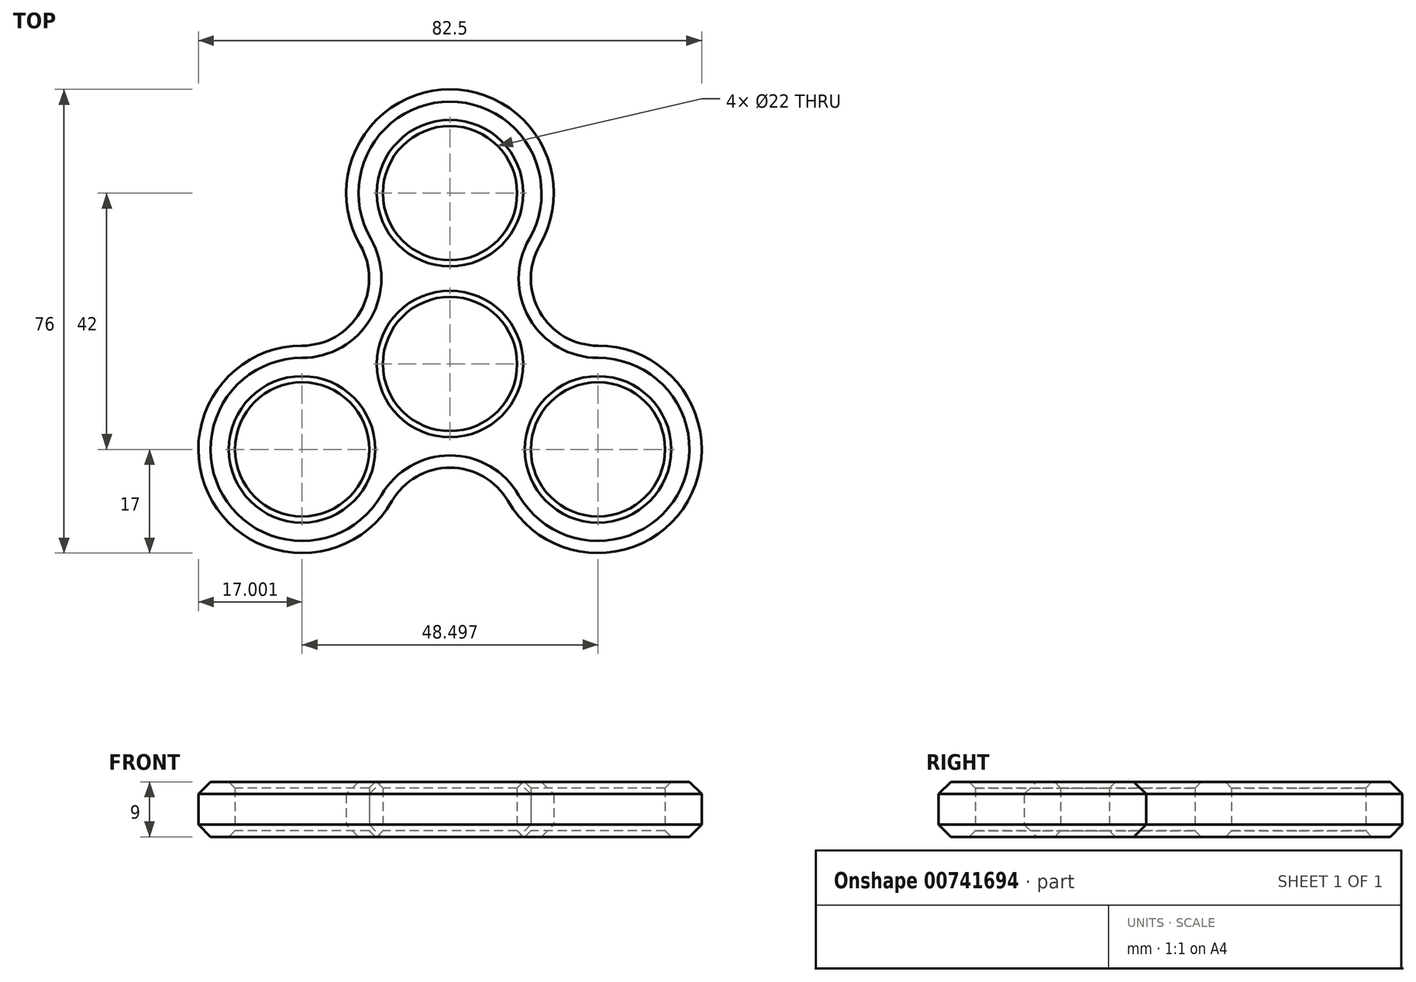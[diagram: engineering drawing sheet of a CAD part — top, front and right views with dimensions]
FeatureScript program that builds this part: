
annotation { "Feature Type Name" : "Feature", "Feature Type Description" : "" }
export const myFeature = defineFeature(function(context is Context, id is Id, definition is map)
    precondition{}
    {
        {
            var Q0;
            Q0=qCreatedBy(makeId("Top.planeOp"),FACE);
            var sketch = newSketch(context, id + "F0", { "sketchPlane" : qUnion([Q0])});
            skCircle(sketch, "E0", {"center": v(0, 28) * mm, "radius": 11 * mm});
            skCircle(sketch, "E1", {"center": v(-24.25, -14) * mm, "radius": 11 * mm});
            skCircle(sketch, "E2", {"center": v(24.25, -14) * mm, "radius": 11 * mm});
            skCircle(sketch, "E3", {"center": v(0, 0) * mm, "radius": 11 * mm});
            skCircle(sketch, "E4", {"center": v(0, 0) * mm, "radius": 28 * mm, "construction": true});
            skLineSegment(sketch, "E5", {"start": v(0, 28) * mm, "end": v(0, 0) * mm, "construction": true});
            skLineSegment(sketch, "E6", {"start": v(0, 0) * mm, "end": v(24.25, -14) * mm, "construction": true});
            skLineSegment(sketch, "E7", {"start": v(0, 0) * mm, "end": v(-24.25, -14) * mm, "construction": true});
            skCircle(sketch, "E8", {"center": v(0, 0) * mm, "radius": 39 * mm, "construction": true});
            skArc(sketch, "E9", {"start": v(-9.53, -22.5) * mm, "mid": v(-38.97, -22.5) * mm, "end": v(-24.25, 3) * mm});
            skArc(sketch, "E10", {"start": v(9.53, -22.5) * mm, "mid": v(38.97, -22.5) * mm, "end": v(24.25, 3) * mm});
            skArc(sketch, "E11", {"start": v(-14.72, 19.5) * mm, "mid": v(0, 45) * mm, "end": v(14.72, 19.5) * mm});
            skLineSegment(sketch, "E12", {"start": v(0, 0) * mm, "end": v(0, -28) * mm, "construction": true});
            skLineSegment(sketch, "E13", {"start": v(0, 0) * mm, "end": v(-24.25, 14) * mm, "construction": true});
            skLineSegment(sketch, "E14", {"start": v(0, 0) * mm, "end": v(24.25, 14) * mm, "construction": true});
            skLineSegment(sketch, "E15", {"start": v(-9.53, -22.5) * mm, "end": v(-9.53, -22.5) * mm});
            skLineSegment(sketch, "E16", {"start": v(-14.72, 19.5) * mm, "end": v(-14.72, 19.5) * mm});
            skLineSegment(sketch, "E17", {"start": v(-24.25, 3) * mm, "end": v(-24.25, 3) * mm});
            skLineSegment(sketch, "E18", {"start": v(14.72, 19.5) * mm, "end": v(14.72, 19.5) * mm});
            skLineSegment(sketch, "E19", {"start": v(24.25, 3) * mm, "end": v(24.25, 3) * mm});
            skLineSegment(sketch, "E20", {"start": v(9.53, -22.5) * mm, "end": v(9.53, -22.5) * mm});
            skArc(sketch, "E21", {"start": v(-14.72, 19.5) * mm, "mid": v(-14.72, 8.5) * mm, "end": v(-24.25, 3) * mm});
            skArc(sketch, "E22", {"start": v(14.72, 19.5) * mm, "mid": v(14.72, 8.5) * mm, "end": v(24.25, 3) * mm});
            skArc(sketch, "E23", {"start": v(9.53, -22.5) * mm, "mid": v(0, -17) * mm, "end": v(-9.53, -22.5) * mm});
            skCircle(sketch, "E24", {"center": v(0, 0) * mm, "radius": 17 * mm, "construction": true});
            skCircle(sketch, "E25", {"center": v(0, 0) * mm, "radius": 45 * mm, "construction": true});
            skSolve(sketch);
        }
        {
            var Q0;
            Q0=qSketchRegion(id+"F0",true);
            extrude(context, id + "F1", {"entities" : qUnion([Q0]), "endBound" : BoundingType.SYMMETRIC, "depth" : 9 * mm, "offsetDistance" : 25 * mm});
        }
        {
            var Q0;
            Q0=qCreatedBy(makeId("Top.planeOp"),FACE);
            var sketch = newSketch(context, id + "F2", { "sketchPlane" : qUnion([Q0])});
            skCircle(sketch, "E26", {"center": v(0, 0) * mm, "radius": 11 * mm});
            skSolve(sketch);
        }
        {
            var Q0;
            Q0=qSketchRegion(id+"F2",true);
            extrude(context, id + "F3", {"entities" : qUnion([Q0]), "operationType" : NewBodyOperationType.REMOVE, "endBound" : BoundingType.THROUGH_ALL, "oppositeDirection" : true, "depth" : 25 * mm, "offsetDistance" : 25 * mm, "hasSecondDirection" : true, "secondDirectionBound" : SecondDirectionBoundingType.THROUGH_ALL, "secondDirectionOppositeDirection" : false, "secondDirectionDepth" : 25 * mm});
        }
        {
            var Q0;
            Q0=makeQuery(id+"F1.opExtrude","CAP_EDGE",EDGE,{"disambiguationData":[OSD([sQuery(id+"F0.wireOp",EDGE,"E9")])],"isStart":false});
            var Q1;
            Q1=makeQuery(id+"F1.opExtrude","CAP_EDGE",EDGE,{"disambiguationData":[OSD([sQuery(id+"F0.wireOp",EDGE,"E9")])],"isStart":true});
            var Q2;
            Q2=makeQuery(id+"F3.boolean.opBoolean","INTERSECT",EDGE,{"derivedFrom":[makeQuery(id+"F1.opExtrude","CAP_FACE",FACE,{"disambiguationData":[OSD([sQuery(id+"F0.wireOp",EDGE,"E0"),sQuery(id+"F0.wireOp",EDGE,"E1"),sQuery(id+"F0.wireOp",EDGE,"E2"),sQuery(id+"F0.wireOp",EDGE,"XNPakRHv-zOhi-0FM5-hTdu-OG3i7tiAVQxY"),sQuery(id+"F0.wireOp",EDGE,"E9"),sQuery(id+"F0.wireOp",EDGE,"dCo0jm6D-gOeC-fFHZ-glrm-1aHonwMQvqJC"),sQuery(id+"F0.wireOp",EDGE,"E10"),sQuery(id+"F0.wireOp",EDGE,"E11"),sQuery(id+"F0.wireOp",EDGE,"YkruY3tB-21v4-OKZR-qZbx-QCQuqMLywjzG"),sQuery(id+"F0.wireOp",EDGE,"SekSoQT0-foV7-ICcH-uNWv-8Mtw90ad5pJT"),sQuery(id+"F0.wireOp",EDGE,"o91gRGPa-Ibxz-ax7s-b3tE-83rfG7TcEAhW"),sQuery(id+"F0.wireOp",EDGE,"bdXiWe1d-0TL7-GA1S-cq4B-UudjERh8iepl")])],"isStart":true}),makeQuery(id+"F3.opExtrude","SWEPT_FACE",FACE,{"disambiguationData":[OSD([sQuery(id+"F2.wireOp",EDGE,"E26")])]})]});
            var Q3;
            Q3=makeQuery(id+"F3.boolean.opBoolean","INTERSECT",EDGE,{"derivedFrom":[makeQuery(id+"F1.opExtrude","CAP_FACE",FACE,{"disambiguationData":[OSD([sQuery(id+"F0.wireOp",EDGE,"E0"),sQuery(id+"F0.wireOp",EDGE,"E1"),sQuery(id+"F0.wireOp",EDGE,"E2"),sQuery(id+"F0.wireOp",EDGE,"XNPakRHv-zOhi-0FM5-hTdu-OG3i7tiAVQxY"),sQuery(id+"F0.wireOp",EDGE,"E9"),sQuery(id+"F0.wireOp",EDGE,"dCo0jm6D-gOeC-fFHZ-glrm-1aHonwMQvqJC"),sQuery(id+"F0.wireOp",EDGE,"E10"),sQuery(id+"F0.wireOp",EDGE,"E11"),sQuery(id+"F0.wireOp",EDGE,"YkruY3tB-21v4-OKZR-qZbx-QCQuqMLywjzG"),sQuery(id+"F0.wireOp",EDGE,"SekSoQT0-foV7-ICcH-uNWv-8Mtw90ad5pJT"),sQuery(id+"F0.wireOp",EDGE,"o91gRGPa-Ibxz-ax7s-b3tE-83rfG7TcEAhW"),sQuery(id+"F0.wireOp",EDGE,"bdXiWe1d-0TL7-GA1S-cq4B-UudjERh8iepl")])],"isStart":false}),makeQuery(id+"F3.opExtrude","SWEPT_FACE",FACE,{"disambiguationData":[OSD([sQuery(id+"F2.wireOp",EDGE,"E26")])]})]});
            chamfer(context, id + "F4", {"entities" : qUnion([Q0, Q1, Q2, Q3]), "width" : 2 * mm, "tangentPropagation" : true});
        }
        {
            var Q0;
            Q0=makeQuery(id+"F1.opExtrude","SWEPT_FACE",FACE,{"disambiguationData":[OSD([sQuery(id+"F0.wireOp",EDGE,"E1")])]});
            var Q1;
            Q1=makeQuery(id+"F1.opExtrude","SWEPT_FACE",FACE,{"disambiguationData":[OSD([sQuery(id+"F0.wireOp",EDGE,"E3")])]});
            var Q2;
            Q2=makeQuery(id+"F1.opExtrude","SWEPT_FACE",FACE,{"disambiguationData":[OSD([sQuery(id+"F0.wireOp",EDGE,"E0")])]});
            var Q3;
            Q3=makeQuery(id+"F1.opExtrude","SWEPT_FACE",FACE,{"disambiguationData":[OSD([sQuery(id+"F0.wireOp",EDGE,"E2")])]});
            chamfer(context, id + "F5", {"entities" : qUnion([Q0, Q1, Q2, Q3]), "width" : 1 * mm, "tangentPropagation" : true});
        }
    });
